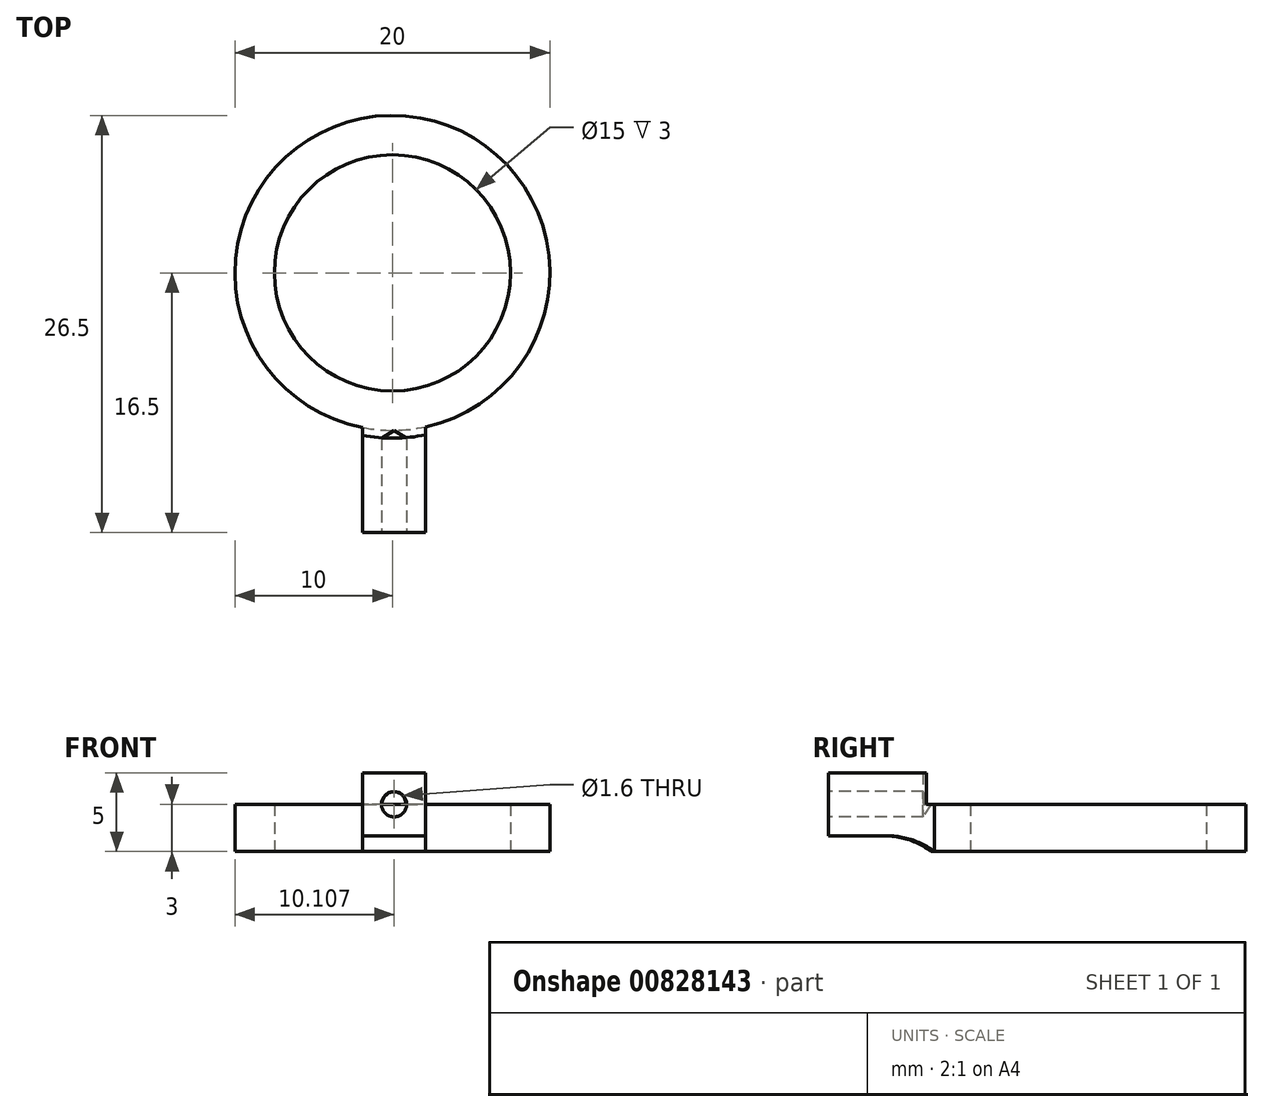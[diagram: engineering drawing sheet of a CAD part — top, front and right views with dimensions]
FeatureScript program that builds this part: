
annotation { "Feature Type Name" : "Feature", "Feature Type Description" : "" }
export const myFeature = defineFeature(function(context is Context, id is Id, definition is map)
    precondition{}
    {
        {
            var Q0;
            Q0=qCreatedBy(makeId("Top.planeOp"),FACE);
            var sketch = newSketch(context, id + "F0", { "sketchPlane" : qUnion([Q0])});
            skCircle(sketch, "E0", {"center": v(0, 0) * mm, "radius": 10 * mm});
            skCircle(sketch, "E1", {"center": v(0, 0) * mm, "radius": 7.5 * mm});
            skSolve(sketch);
        }
        {
            var Q0;
            Q0 = qSketchRegion(id + "F0", true);
            extrude(context, id + "F1", {"entities" : qUnion([Q0]), "depth" : 3 * mm, "offsetDistance" : 25 * mm});
        }
        {
            var Q0;
            Q0=qCreatedBy(makeId("Top.planeOp"),FACE);
            cPlane(context, id + "F2", {"entities" : qUnion([Q0]), "cplaneType" : CPlaneType.OFFSET, "offset" : 1 * mm, "width" : 150 * mm, "height" : 150 * mm});
        }
        {
            var Q0;
            Q0=qCreatedBy(id+"F2.planeOp",FACE);
            var sketch = newSketch(context, id + "F3", { "sketchPlane" : qUnion([Q0])});
            skLineSegment(sketch, "E2.bottom", {"start": v(-1.9, -9.5) * mm, "end": v(2.1, -9.5) * mm});
            skLineSegment(sketch, "E2.top", {"start": v(-1.9, -16.5) * mm, "end": v(2.1, -16.5) * mm});
            skLineSegment(sketch, "E2.left", {"start": v(-1.9, -9.5) * mm, "end": v(-1.9, -16.5) * mm});
            skLineSegment(sketch, "E2.right", {"start": v(2.1, -9.5) * mm, "end": v(2.1, -16.5) * mm});
            skSolve(sketch);
        }
        {
            var Q0;
            Q0 = qSketchRegion(id + "F3", true);
            extrude(context, id + "F4", {"entities" : qUnion([Q0]), "operationType" : NewBodyOperationType.ADD, "depth" : 4 * mm, "offsetDistance" : 25 * mm});
        }
        {
            var Q0;
            Q0=makeQuery(id+"F1.opExtrude","CAP_FACE",FACE,{"disambiguationData":[OSD([sQuery(id+"F0.wireOp",EDGE,"E0"),sQuery(id+"F0.wireOp",EDGE,"E1")])],"isStart":false});
            var sketch = newSketch(context, id + "F5", { "sketchPlane" : qUnion([Q0])});
            skCircle(sketch, "E3", {"center": v(0, 0) * mm, "radius": 10.5 * mm});
            skSolve(sketch);
        }
        {
            var Q0;
            Q0 = qSketchRegion(id + "F5", true);
            extrude(context, id + "F6", {"entities" : qUnion([Q0]), "operationType" : NewBodyOperationType.REMOVE, "depth" : 25 * mm, "offsetDistance" : 25 * mm});
        }
        {
            var Q0;
            Q0=makeQuery(id+"F4.boolean.opBoolean","INTERSECT",EDGE,{"derivedFrom":[makeQuery(id+"F1.opExtrude","SWEPT_FACE",FACE,{"disambiguationData":[OSD([sQuery(id+"F0.wireOp",EDGE,"E0")])]}),makeQuery(id+"F4.opExtrude","CAP_FACE",FACE,{"disambiguationData":[OSD([sQuery(id+"F3.wireOp",EDGE,"E2.bottom"),sQuery(id+"F3.wireOp",EDGE,"E2.top"),sQuery(id+"F3.wireOp",EDGE,"E2.left"),sQuery(id+"F3.wireOp",EDGE,"E2.right")])],"isStart":true})]});
            fillet(context, id + "F7", {"entities" : qUnion([Q0]), "radius" : 5 * mm, "tangentPropagation" : true, "allowEdgeOverflow" : false});
        }
        {
            var Q0;
            Q0=makeQuery(id+"F4.opExtrude","SWEPT_FACE",FACE,{"disambiguationData":[OSD([sQuery(id+"F3.wireOp",EDGE,"E2.top")])]});
            var sketch = newSketch(context, id + "F8", { "sketchPlane" : qUnion([Q0])});
            skLineSegment(sketch, "E4", {"start": v(0.1, 5) * mm, "end": v(0.1, 1) * mm, "construction": true});
            skPoint(sketch, "E5", {"position": v(0.1, 3) * mm});
            skSolve(sketch);
        }
        {
            var Q0;
            Q0=sQuery(id+"F8.wireOp",VERTEX,"E5");
            var Q1;
            Q1=makeQuery(id+"F1.opExtrude","SWEPT_BODY",BODY,{"disambiguationData":[OSD([sQuery(id+"F0.wireOp",EDGE,"E0"),sQuery(id+"F0.wireOp",EDGE,"E1")])]});
            hole(context, id + "F9", {"style" : HoleStyle.SIMPLE, "endStyle" : HoleEndStyle.BLIND, "holeDiameter" : 1.6 * mm, "majorDiameter" : 5 * mm, "holeDepth" : 6 * mm, "isTappedThrough" : true, "tappedDepth" : 7.3 * mm, "tapClearance" : 3, "locations" : qUnion([Q0]), "scope" : qUnion([Q1])});
        }
    });
